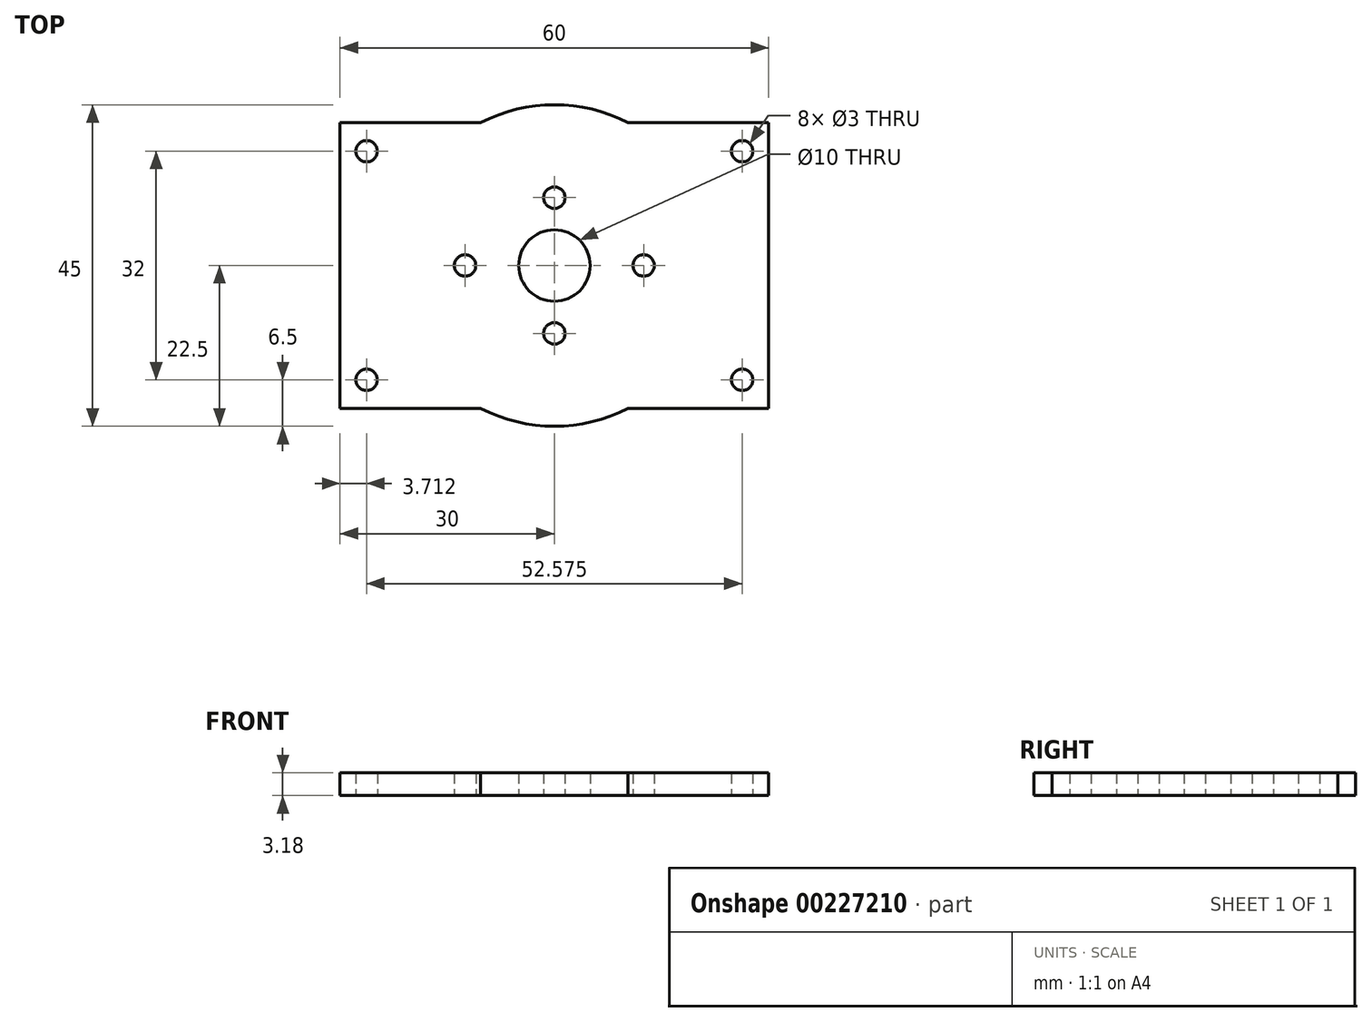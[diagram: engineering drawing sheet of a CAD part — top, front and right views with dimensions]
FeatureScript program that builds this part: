
annotation { "Feature Type Name" : "Feature", "Feature Type Description" : "" }
export const myFeature = defineFeature(function(context is Context, id is Id, definition is map)
    precondition{}
    {
        {
            var Q0;
            Q0=qCreatedBy(makeId("Top.planeOp"),FACE);
            var sketch = newSketch(context, id + "F0", { "sketchPlane" : qUnion([Q0])});
            skLineSegment(sketch, "E0.bottom", {"start": v(30, -20) * mm, "end": v(-30, -20) * mm});
            skLineSegment(sketch, "E0.top", {"start": v(30, 20) * mm, "end": v(-30, 20) * mm});
            skLineSegment(sketch, "E0.left", {"start": v(30, -20) * mm, "end": v(30, 20) * mm});
            skLineSegment(sketch, "E0.right", {"start": v(-30, -20) * mm, "end": v(-30, 20) * mm});
            skPoint(sketch, "E0.middle", {"position": v(0, 0) * mm});
            skCircle(sketch, "E1", {"center": v(0, 0) * mm, "radius": 22.5 * mm});
            skCircle(sketch, "E2", {"center": v(-26.29, 16) * mm, "radius": 1.5 * mm});
            skCircle(sketch, "E3.MirrorC", {"center": v(-26.29, -16) * mm, "radius": 1.5 * mm});
            skCircle(sketch, "E4.MirrorC", {"center": v(26.29, 16) * mm, "radius": 1.5 * mm});
            skCircle(sketch, "E5.MirrorC", {"center": v(26.29, -16) * mm, "radius": 1.5 * mm});
            skCircle(sketch, "E6", {"center": v(0, 0) * mm, "radius": 5 * mm});
            skCircle(sketch, "E7", {"center": v(0, 9.5) * mm, "radius": 1.5 * mm});
            skCircle(sketch, "E8.MirrorC", {"center": v(0, -9.5) * mm, "radius": 1.5 * mm});
            skCircle(sketch, "E9", {"center": v(-12.5, 0) * mm, "radius": 1.5 * mm});
            skCircle(sketch, "E10.MirrorC", {"center": v(12.5, 0) * mm, "radius": 1.5 * mm});
            skSolve(sketch);
        }
        {
            var Q0;
            Q0 = qSketchRegion(id + "F0", true);
            extrude(context, id + "F1", {"entities" : qUnion([Q0]), "depth" : 3.17 * mm});
        }
    });
